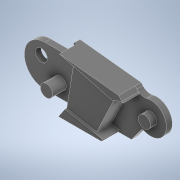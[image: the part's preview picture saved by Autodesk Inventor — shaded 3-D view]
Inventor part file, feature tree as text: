
AUTODESK INVENTOR PART (.ipt)
format: ipt  version: 2022 (Build 260153000, 153)  size: 393,728 bytes
history: native  units: in
note: dims shown in document units (in); Inventor stores cm internally (conversion verified against a paired STEP export)
features: extrude x5, sketch x5, other x1
ambient origin geometry x8: Origin, YZ Plane, XZ Plane, XY Plane, X Axis, Y Axis, Z Axis, Center Point
bodies: Body1 (feature_tree)
feature tree (11):
  other  "Sólido1"
  extrude  "Extrusión1"  Depth=0.0984in
  extrude  "Extrusión2"  Depth=0.1339in TaperAngle=0.0deg
  extrude  "Extrusión3"  Depth=0.0591in TaperAngle=0.0deg
  extrude  "Extrusión4"  Depth=0.1181in TaperAngle=0.0deg
  extrude  "Extrusión6"  [1 undecoded]
  sketch  "Boceto1"  dims[d1=0.0984in d6=0.3307in]
  sketch  "Boceto2"  dims[d18=0.0472in d19=0.0in d24=0.1339in d25=0.0in]
  sketch  "Boceto3"  dims[d26=0.0984in d27=0.0in d28=0.0591in d29=0.0in]
  sketch  "Boceto4"  dims[d33=0.0787in d34=0.1181in d35=0.0in]
  sketch  "Boceto6"
note: 1 required parameter value undecoded (feature->parameter linkage not recoverable at this tier; creation-order binding heuristic only, values carry confidence <= 0.55)
